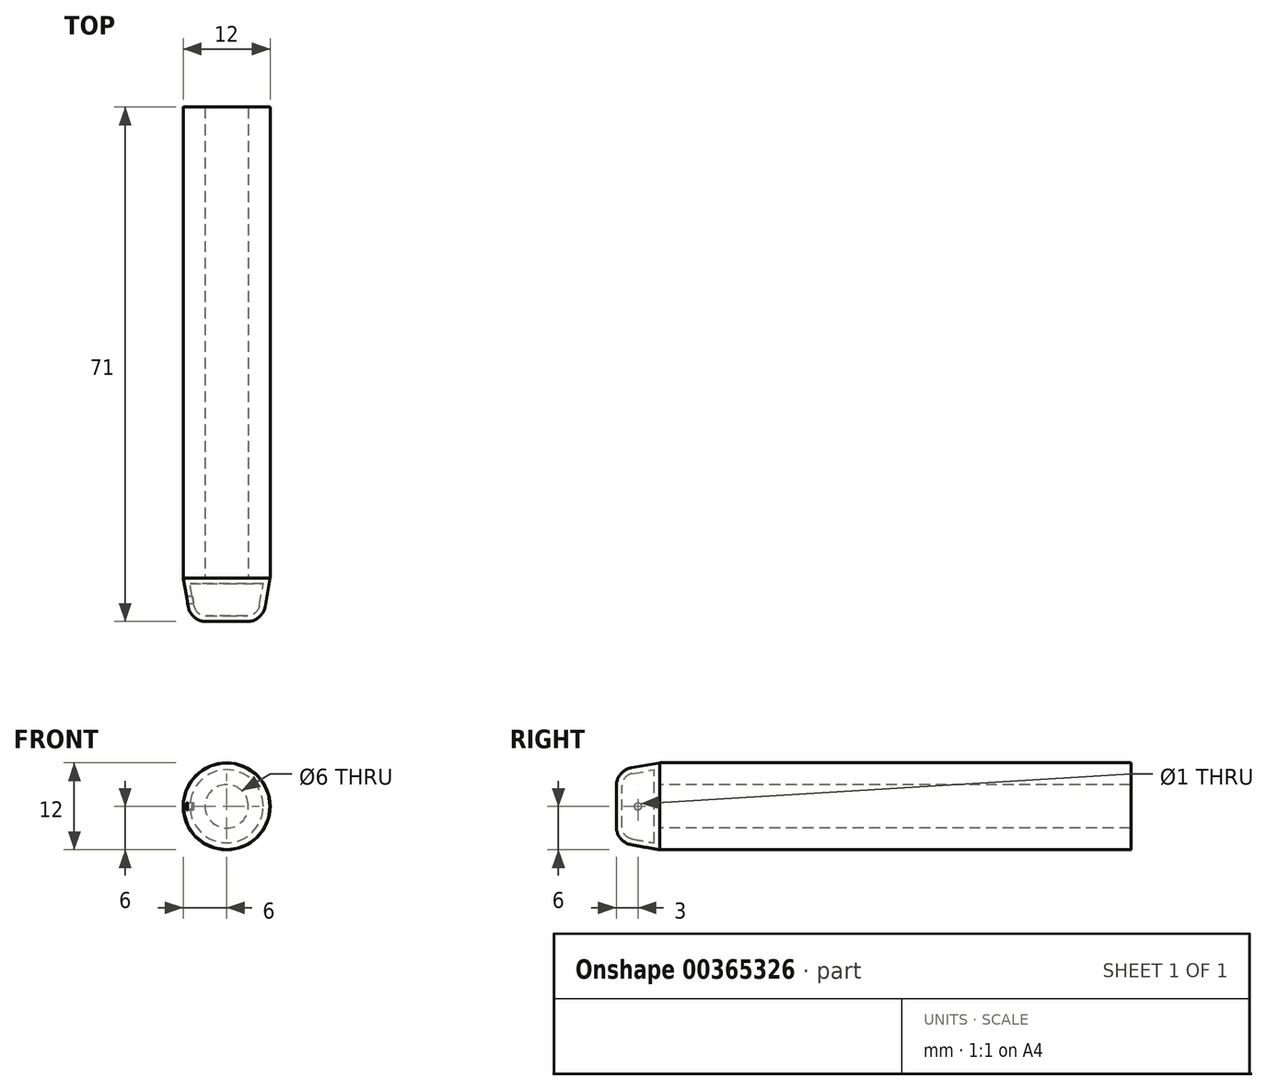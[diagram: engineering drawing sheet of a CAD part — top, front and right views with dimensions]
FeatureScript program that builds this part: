
annotation { "Feature Type Name" : "Feature", "Feature Type Description" : "" }
export const myFeature = defineFeature(function(context is Context, id is Id, definition is map)
    precondition{}
    {
        {
            var Q0;
            Q0=qCreatedBy(makeId("Front.planeOp"),FACE);
            var sketch = newSketch(context, id + "F0", { "sketchPlane" : qUnion([Q0])});
            skCircle(sketch, "E0", {"center": v(0, 0) * mm, "radius": 3 * mm});
            skCircle(sketch, "E1", {"center": v(0, 0) * mm, "radius": 6 * mm});
            skSolve(sketch);
        }
        {
            var Q0;
            Q0 = qSketchRegion(id + "F0", true);
            extrude(context, id + "F1", {"entities" : qUnion([Q0]), "oppositeDirection" : true, "depth" : 65 * mm});
        }
        {
            var Q0;
            Q0 = qSketchRegion(id + "F0", true);
            var Q1;
            Q1=makeQuery(id+"F0.imprint","IMPRINT",FACE,{"disambiguationData":[TD([[makeQuery(id+"F0.imprint","IMPRINT",EDGE,{"derivedFrom":sQuery(id+"F0.wireOp",EDGE,"E0")}),1.0]])]});
            extrude(context, id + "F2", {"entities" : qUnion([Q0, Q1]), "depth" : 6 * mm, "hasDraft" : true, "draftAngle" : 10 * degree, "draftPullDirection" : true});
        }
        {
            var Q0;
            Q0=makeQuery(id+"F2.opExtrude","CAP_EDGE",EDGE,{"disambiguationData":[OSD([sQuery(id+"F0.wireOp",EDGE,"E1")])],"isStart":false});
            fillet(context, id + "F3", {"entities" : qUnion([Q0]), "radius" : 2.5 * mm, "tangentPropagation" : true, "allowEdgeOverflow" : false});
        }
        {
            var Q0;
            Q0=makeQuery(id+"F2.opExtrude","CAP_FACE",FACE,{"disambiguationData":[OSD([sQuery(id+"F0.wireOp",EDGE,"E1")])],"isStart":true});
            var Q1;
            Q1=makeQuery(id+"F2.opExtrude","SWEPT_BODY",BODY,{"disambiguationData":[OSD([sQuery(id+"F0.wireOp",EDGE,"E1")])]});
            shell(context, id + "F4", {"isHollow" : true, "entities" : qUnion([Q0]), "parts" : qUnion([Q1]), "thickness" : 0.8 * mm});
        }
        {
            var Q0;
            Q0=qCreatedBy(makeId("Right.planeOp"),FACE);
            var sketch = newSketch(context, id + "F5", { "sketchPlane" : qUnion([Q0])});
            skCircle(sketch, "E2", {"center": v(-3, 0) * mm, "radius": 0.5 * mm});
            skSolve(sketch);
        }
        {
            var Q0;
            Q0 = qSketchRegion(id + "F5", true);
            var Q1;
            Q1=makeQuery(id+"F2.opExtrude","SWEPT_FACE",FACE,{"disambiguationData":[OSD([sQuery(id+"F0.wireOp",EDGE,"E1")])]});
            extrude(context, id + "F6", {"entities" : qUnion([Q0]), "operationType" : NewBodyOperationType.REMOVE, "endBound" : BoundingType.UP_TO_SURFACE, "oppositeDirection" : true, "endBoundEntityFace" : qUnion([Q1]), "depth" : 25 * mm});
        }
        {
            var Q0;
            Q0=makeQuery(id+"F1.opExtrude","SWEPT_FACE",FACE,{"disambiguationData":[OSD([sQuery(id+"F0.wireOp",EDGE,"E1")])]});
            var Q1;
            Q1=makeQuery(id+"F1.opExtrude","SWEPT_FACE",FACE,{"disambiguationData":[OSD([sQuery(id+"F0.wireOp",EDGE,"E0")])]});
            var Q2;
            Q2=makeQuery(id+"F2.opExtrude","CAP_FACE",FACE,{"disambiguationData":[OSD([sQuery(id+"F0.wireOp",EDGE,"E1")])],"isStart":true});
            fillet(context, id + "F7", {"entities" : qUnion([Q0, Q1, Q2]), "radius" : 0.1 * mm, "tangentPropagation" : true, "allowEdgeOverflow" : false});
        }
    });
